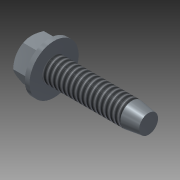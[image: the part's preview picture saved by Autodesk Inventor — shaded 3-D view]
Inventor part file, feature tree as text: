
AUTODESK INVENTOR PART (.ipt)
format: ipt  version: 2014 (Build 180170000, 170)  size: 167,936 bytes
history: native  units: mm (DEFAULTED — no unit token found)
features: sketch x4, extrude x2, other x1, chamfer x1, plane x1
ambient origin geometry x8: Origin, YZ Plane, XZ Plane, XY Plane, X Axis, Y Axis, Z Axis, Center Point
bodies: Solid1 (feature_tree), Body (feature_tree)
feature tree (9):
  extrude  "Head"  Depth=1.27mm
  other  "IDS_WORKPLANE{1}"
  extrude  "Indent"  TaperAngle=90.0deg  [1 undecoded]
  chamfer  "Chamfer1"  [1 undecoded]
  plane  "Work Plane3"
  sketch  "Sketch1"  dims[d1=1.27mm d2=6.35mm]
  sketch  "Sketch2"  dims[d3=25.4mm d77=90.0deg]
  sketch  "Sketch3"  dims[d6=25.4mm]
  sketch  "Sketch4"  dims[d7=0.0mm d10=0.0mm d11=9.525mm d12=4.826mm d13=0.0mm d14=0.0mm d15=7.62mm d16=0.4826mm d17=0.0mm d92=90.0deg d19=0.635mm d20=4.445mm d21=9.525mm d22=13.208mm d23=8.248892mm d98=45.0deg d99=0.0mm d100=0.0mm]
note: 2 required parameter values undecoded (feature->parameter linkage not recoverable at this tier; creation-order binding heuristic only, values carry confidence <= 0.55)
